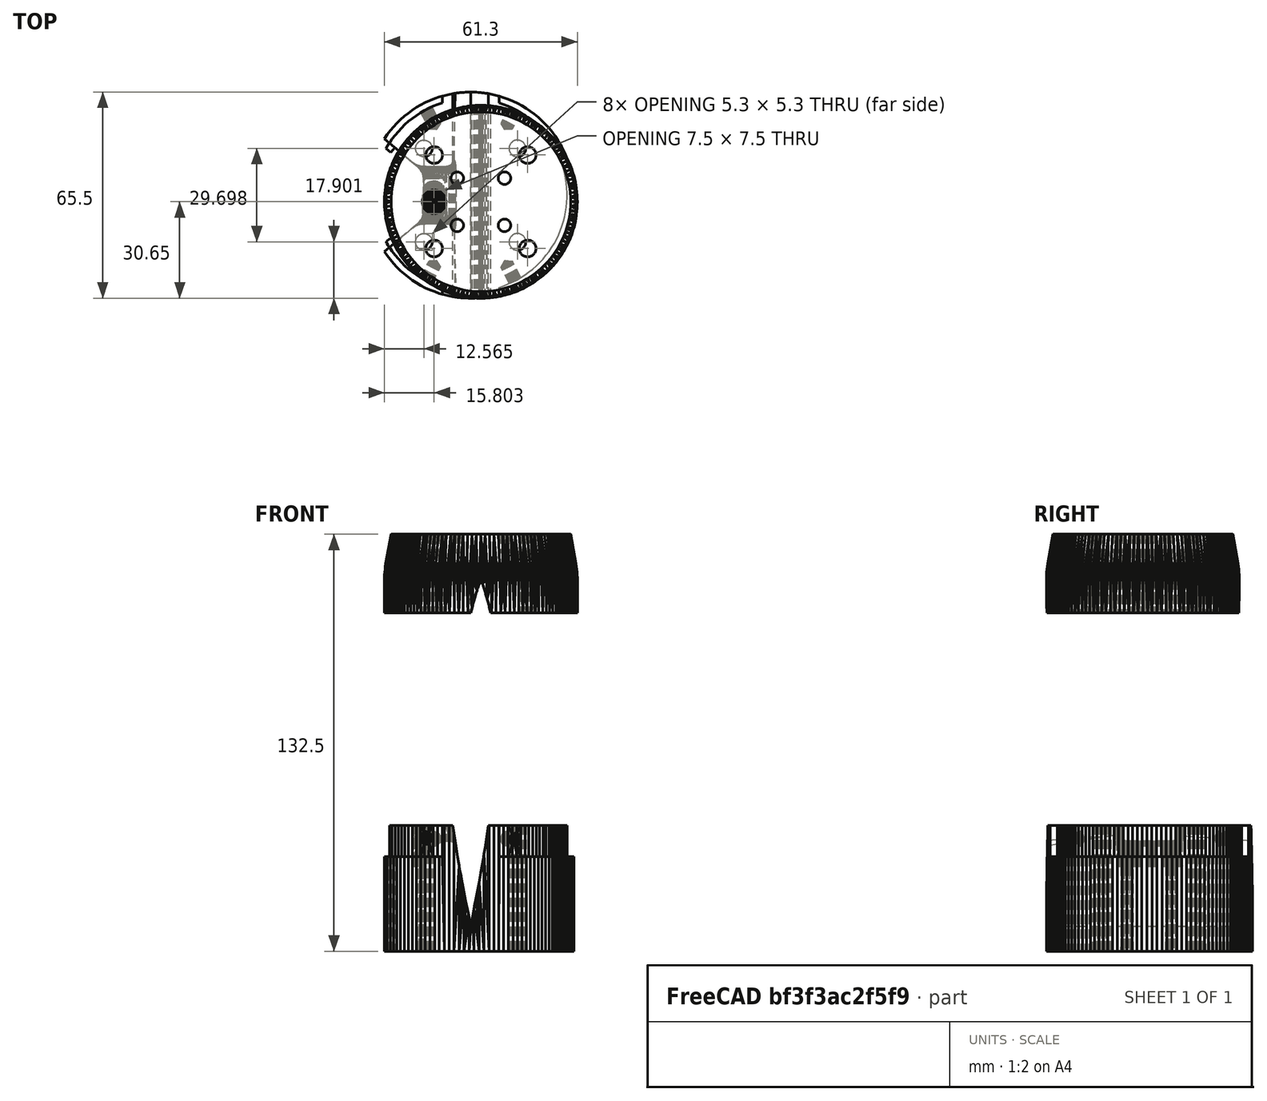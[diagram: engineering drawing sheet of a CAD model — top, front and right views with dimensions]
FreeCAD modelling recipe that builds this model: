
FCSTD DOCUMENT  (FreeCAD 0.21R33771 (Git))
Label: motor hold
License: All rights reserved
LicenseURL: http://en.wikipedia.org/wiki/All_rights_reserved
objects: Part::Refine×3, Mesh::Feature×3, Part::Feature×2, PartDesign::FeatureBase×2, PartDesign::Body×2, App::Part×1
note: 9 computed .brp shape members not serialized (recipe doc carries the construction recipe); baked Part::Feature solids carry a one-line shape summary decoded from their .brp

FEATURE [Part::Feature] Fore_mast_clamp_v005_solid  label="Fore_mast_clamp_v005 (Solid)"
  shape: bbox 61.3 x 61.3 x 25 mm, 6348 faces (baked)
FEATURE [Part::Refine] Fore_mast_clamp_v005_solid001  label="Fore_mast_clamp_v005 (Solid)001"
  Source = -> Fore_mast_clamp_v005_solid
FEATURE [PartDesign::FeatureBase] BaseFeature
  BaseFeature = -> Fore_mast_clamp_v005_solid001
FEATURE [PartDesign::Body] Body
  BaseFeature = -> Fore_mast_clamp_v005_solid001
  Group = -> [BaseFeature]
  Origin = -> Origin001
  Tip = -> BaseFeature
FEATURE [Part::Feature] Nose_cone_v005_solid  label="Nose_cone_v005 (Solid)"
  shape: bbox 65.49 x 65.5 x 154.5 mm, 26990 faces (baked)
FEATURE [Part::Refine] Nose_cone_v005_solid001  label="Nose_cone_v005 (Solid)001"
  Source = -> Nose_cone_v005_solid
FEATURE [PartDesign::FeatureBase] BaseFeature001
  BaseFeature = -> Nose_cone_v005_solid001
FEATURE [PartDesign::Body] Body001
  BaseFeature = -> Nose_cone_v005_solid001
  Group = -> [BaseFeature001]
  Origin = -> Origin002
  Placement = pos=(-2.54,-2.54,107.95) rot=(0,0,1;0rad)
  Tip = -> BaseFeature001
FEATURE [App::Part] Part
  Group = -> [Fore_mast_clamp_v005_solid,Fore_mast_clamp_v005_solid001,Body,Nose_cone_v005_solid001,Nose_cone_v005_solid,Body001]
  Origin = -> Origin
FEATURE [Mesh::Feature] Aft_mast_clamp_v4
FEATURE [Part::Refine] Aft_mast_clamp_v005_solid001  label="Aft_mast_clamp_v005 (Solid)001"
FEATURE [Mesh::Feature] Cable_cover_v4_1  label="Cable_cover_v4.1"
  Placement = pos=(-83.82,0,0) rot=(0,0,1;0rad)
FEATURE [Mesh::Feature] Nose_cone_v4
  Placement = pos=(0,0,99.06) rot=(0,0,1;0rad)
